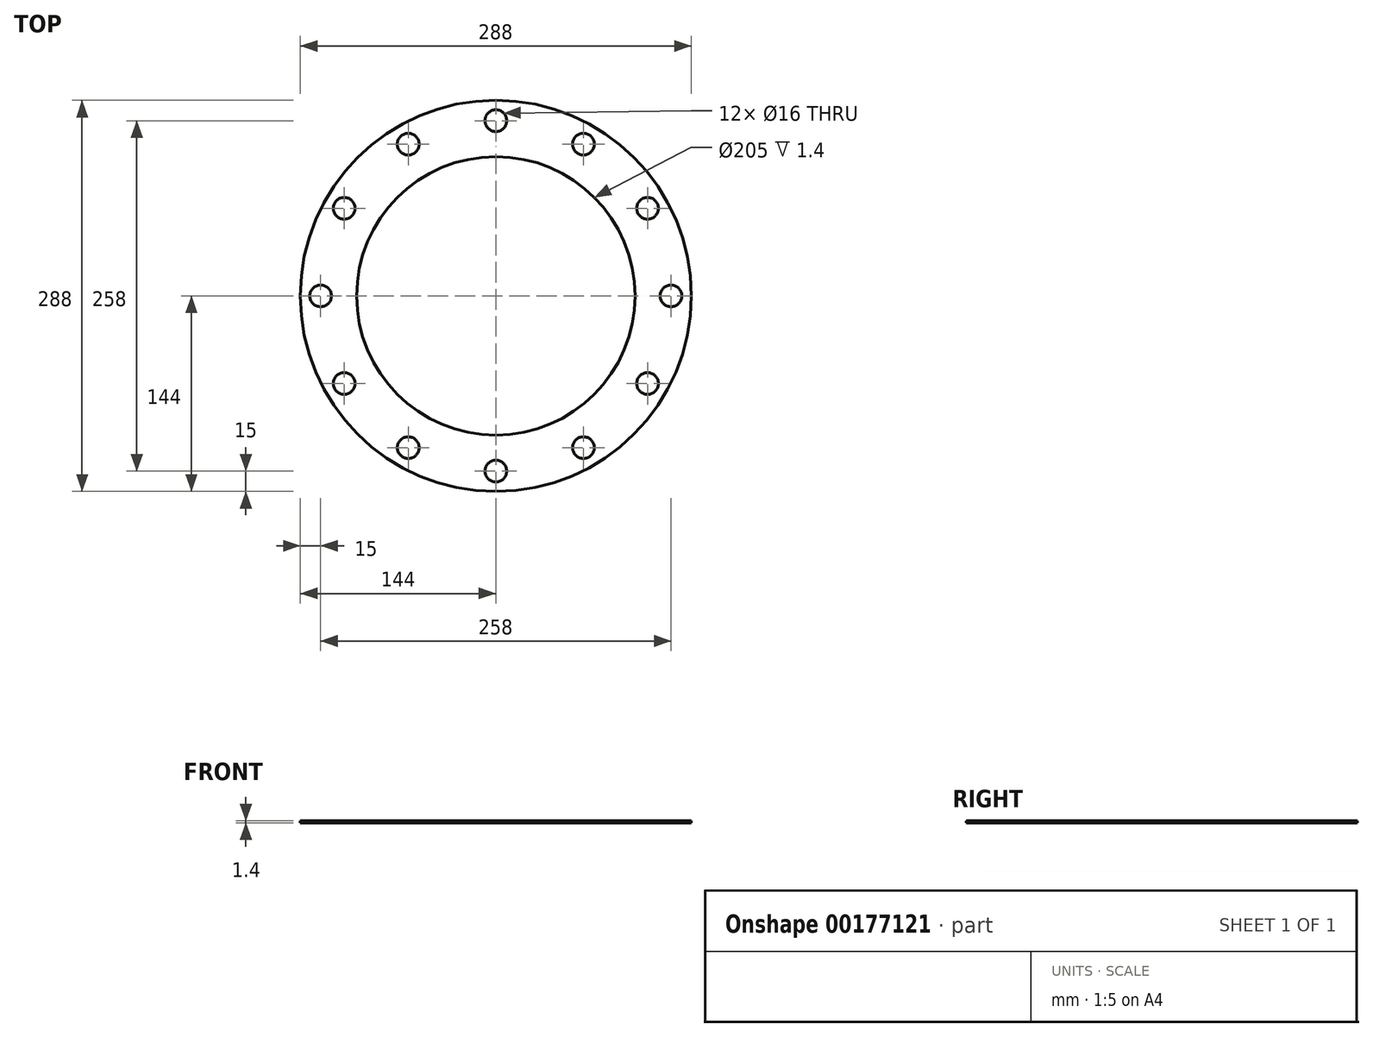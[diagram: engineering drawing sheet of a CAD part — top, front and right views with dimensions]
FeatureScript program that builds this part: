
annotation { "Feature Type Name" : "Feature", "Feature Type Description" : "" }
export const myFeature = defineFeature(function(context is Context, id is Id, definition is map)
    precondition{}
    {
        {
            var Q0;
            Q0=qCreatedBy(makeId("Top.planeOp"),FACE);
            var sketch = newSketch(context, id + "F0", { "sketchPlane" : qUnion([Q0])});
            skCircle(sketch, "E0", {"center": v(0, 0) * mm, "radius": 144 * mm});
            skCircle(sketch, "E1", {"center": v(0, 0) * mm, "radius": 129 * mm, "construction": true});
            skCircle(sketch, "E2", {"center": v(0, 129) * mm, "radius": 8 * mm});
            skCircle(sketch, "E3", {"center": v(64.5, 111.72) * mm, "radius": 8 * mm});
            skCircle(sketch, "E4", {"center": v(111.72, 64.5) * mm, "radius": 8 * mm});
            skLineSegment(sketch, "E5", {"start": v(0, 129) * mm, "end": v(0, 0) * mm, "construction": true});
            skLineSegment(sketch, "E6", {"start": v(64.5, 111.72) * mm, "end": v(0, 0) * mm, "construction": true});
            skLineSegment(sketch, "E7", {"start": v(0, 0) * mm, "end": v(111.72, 64.5) * mm, "construction": true});
            skCircle(sketch, "E8", {"center": v(64.5, -111.72) * mm, "radius": 8 * mm});
            skCircle(sketch, "E9", {"center": v(111.72, -64.5) * mm, "radius": 8 * mm});
            skCircle(sketch, "E10", {"center": v(-64.5, 111.72) * mm, "radius": 8 * mm});
            skCircle(sketch, "E11", {"center": v(-111.72, 64.5) * mm, "radius": 8 * mm});
            skCircle(sketch, "E12", {"center": v(-111.72, -64.5) * mm, "radius": 8 * mm});
            skCircle(sketch, "E13", {"center": v(0, -129) * mm, "radius": 8 * mm});
            skCircle(sketch, "E14", {"center": v(-129, 0) * mm, "radius": 8 * mm});
            skCircle(sketch, "E15", {"center": v(129, 0) * mm, "radius": 8 * mm});
            skLineSegment(sketch, "E16", {"start": v(0, 0) * mm, "end": v(-129, 0) * mm, "construction": true});
            skLineSegment(sketch, "E17", {"start": v(0, 0) * mm, "end": v(-111.72, 64.5) * mm, "construction": true});
            skLineSegment(sketch, "E18", {"start": v(0, 0) * mm, "end": v(129, 0) * mm, "construction": true});
            skLineSegment(sketch, "E19", {"start": v(0, 0) * mm, "end": v(0, -129) * mm, "construction": true});
            skLineSegment(sketch, "E20", {"start": v(0, 0) * mm, "end": v(-111.72, -64.5) * mm, "construction": true});
            skLineSegment(sketch, "E21", {"start": v(0, 0) * mm, "end": v(64.5, -111.72) * mm, "construction": true});
            skLineSegment(sketch, "E22", {"start": v(0, 0) * mm, "end": v(-64.5, 111.72) * mm, "construction": true});
            skLineSegment(sketch, "E23", {"start": v(111.72, -64.5) * mm, "end": v(0, 0) * mm, "construction": true});
            skCircle(sketch, "E24", {"center": v(-64.5, -111.72) * mm, "radius": 8 * mm});
            skLineSegment(sketch, "E25", {"start": v(-64.5, -111.72) * mm, "end": v(0, 0) * mm, "construction": true});
            skCircle(sketch, "E26", {"center": v(0, 0) * mm, "radius": 102.5 * mm});
            skSolve(sketch);
        }
        {
            var Q0;
            Q0=makeQuery(id+"F0.imprint","IMPRINT",FACE,{"disambiguationData":[TD([[makeQuery(id+"F0.imprint","IMPRINT",EDGE,{"derivedFrom":sQuery(id+"F0.wireOp",EDGE,"E0")}),1.0]])]});
            extrude(context, id + "F1", {"entities" : qUnion([Q0]), "depth" : 1.4 * mm});
        }
    });
